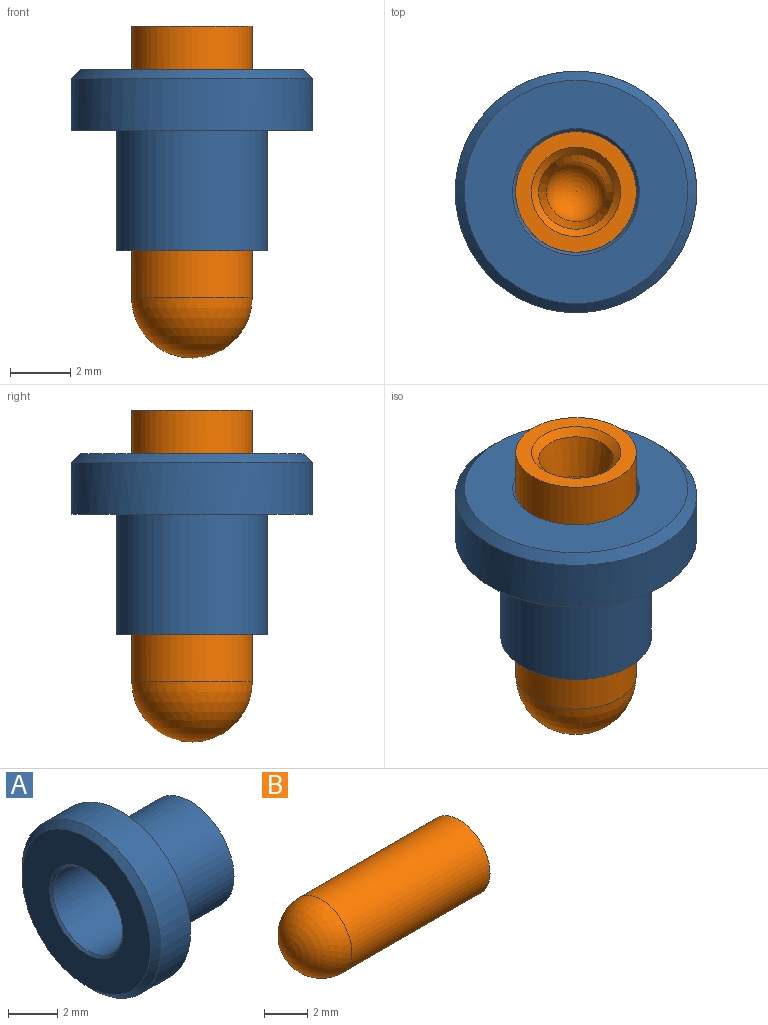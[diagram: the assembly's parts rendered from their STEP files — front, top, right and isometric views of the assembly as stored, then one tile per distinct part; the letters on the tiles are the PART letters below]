
ASSEMBLY  parts=2 mates=1
PART A: 8 faces, bbox 6x8x8 mm
  f0: plane 5x5mm, normal (1,0,0), area 7.1mm2, adj f1,f5
  f1: cylinder r=2mm len=5.9mm, axis (-1,0,0), area 74.1mm2, adj f0,f7
  f2: plane 7.4x7.4mm, normal (-1,0,0), area 29.2mm2, adj f6,f7
  f3: cylinder r=4mm len=8mm, axis (-1,0,0), area 42.7mm2, adj f4,f6
  f4: plane 8x8mm, normal (1,0,0), area 30.6mm2, adj f3,f5
  f5: cylinder r=2.5mm len=5mm, axis (-1,0,0), area 62.8mm2, adj f0,f4
  f6: cone r=3.7mm half-angle=45deg, axis (1,0,0), area 10.3mm2, adj f2,f3
  f7: cone r=2mm half-angle=45deg, axis (-1,0,0), area 1.8mm2, adj f1,f2
PART B: 6 faces, bbox 11x4x4 mm
  f0: cylinder r=2mm len=9mm, axis (-1,0,0), area 113.1mm2, adj f1,f5
  f1: plane 4x4mm, normal (1,0,0), area 5.7mm2, adj f0,f4
  f2: cone r=1.28mm half-angle=10deg, axis (1,0,0), area 10.1mm2, adj f3,f4
  f3: sphere r=1mm, area 5.2mm2, adj f2
  f4: cone r=1.24mm half-angle=45deg, axis (1,0,0), area 2.9mm2, adj f1,f2
  f5: sphere r=2mm, area 25.1mm2, adj f0
PLACE A rot(axis=(0,1,0),90deg) t=(0,0,2)mm
PLACE B rot(axis=(0,-1,0),90deg) t=(0,0,1.95)mm
MATE slider B.f0 <-> A.f1  axis (0,0,-1) through (0,0,-1.05)mm
